# Revit family: Bath-Drop_In-KOHLER-TEA_FOR_TWO -K-855T
name_source: partatom
category: Plumbing Fixtures
revit_build: Autodesk Revit 2017 (Build: 20160225_1515(x64)
units: mm (PartAtom-declared; Revit-internal decimal feet)

## family parameters
Cut with Voids When Loaded = No
Host = Face
OmniClass Number = 23.31.15.00
OmniClass Title = Bathtubs
Part Type = Normal
Room Calculation Point = No
Round Connector Dimension = Use Diameter
Shared = No

## types (1)
- 0-White
    ADA Compliant = No
    Assembly Code = D2010500
    CW Connection = No
    Cold Water Inlet = Cold Water Inlet
    Date Modified = 01/29/2021
    Default Elevation = 0"
    Description = 5.5' CAST IRON BATH
    Drain Included = Yes
    Finish = Kohler-Enameled_Cast_Iron-0-White
    HW Connection = No
    Height = 24"
    Hot Water Inlet = Hot Water Inlet
    Length = 66"
    Manufacturer = KOHLER Co.
    MasterFormat 1995 = 15410
    MasterFormat 2004 = 22.41.19
    Material = Enameled cast iron
    Model = K-855T-0
    Product Documentation Link = https://files.kohler.com.cn
    Product Name = TEA FOR TWO
    Product Page URL = https://www.kohler.com.cn
    Type = 1
    URL = http://www.kohler.com.cn
    Vent Connection = No
    Waste Connection = Yes
    Waste Water Outlet = Waste Water Outlet
    Width = 36"

## geometry (parser evidence)
native form markers: Sweep x4
no freeform markers — native parametric forms only
